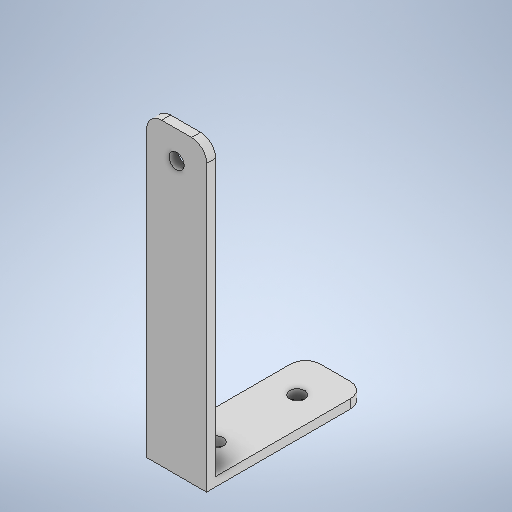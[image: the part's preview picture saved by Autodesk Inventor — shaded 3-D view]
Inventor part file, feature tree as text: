
AUTODESK INVENTOR PART (.ipt)
format: ipt  version: 2025.1 (Build 291241020, 241B)  size: 273,408 bytes
history: native  units: mm
features: extrude x2, fillet x2, sketch x2
ambient origin geometry x8: Origin, YZ Plane, XZ Plane, XY Plane, X Axis, Y Axis, Z Axis, Center Point
bodies: Solid1 (feature_tree)
feature tree (6):
  extrude  "Extrusion1"  Depth=50.0mm
  extrude  "Extrusion2"  Depth=5.0mm
  fillet  "Fillet1"  Radius=3.0mm
  fillet  "Fillet2"  Radius=20.0mm
  sketch  "Sketch1"  dims[d0=20.0mm d1=50.0mm]
  sketch  "Sketch2"  dims[d2=5.0mm d3=5.0mm d4=3.0mm d5=0.0mm d6=20.0mm d7=100.0mm d8=5.1mm d9=90.706mm d19=3.0mm d20=0.0mm d21=5.0mm d22=5.0mm]
